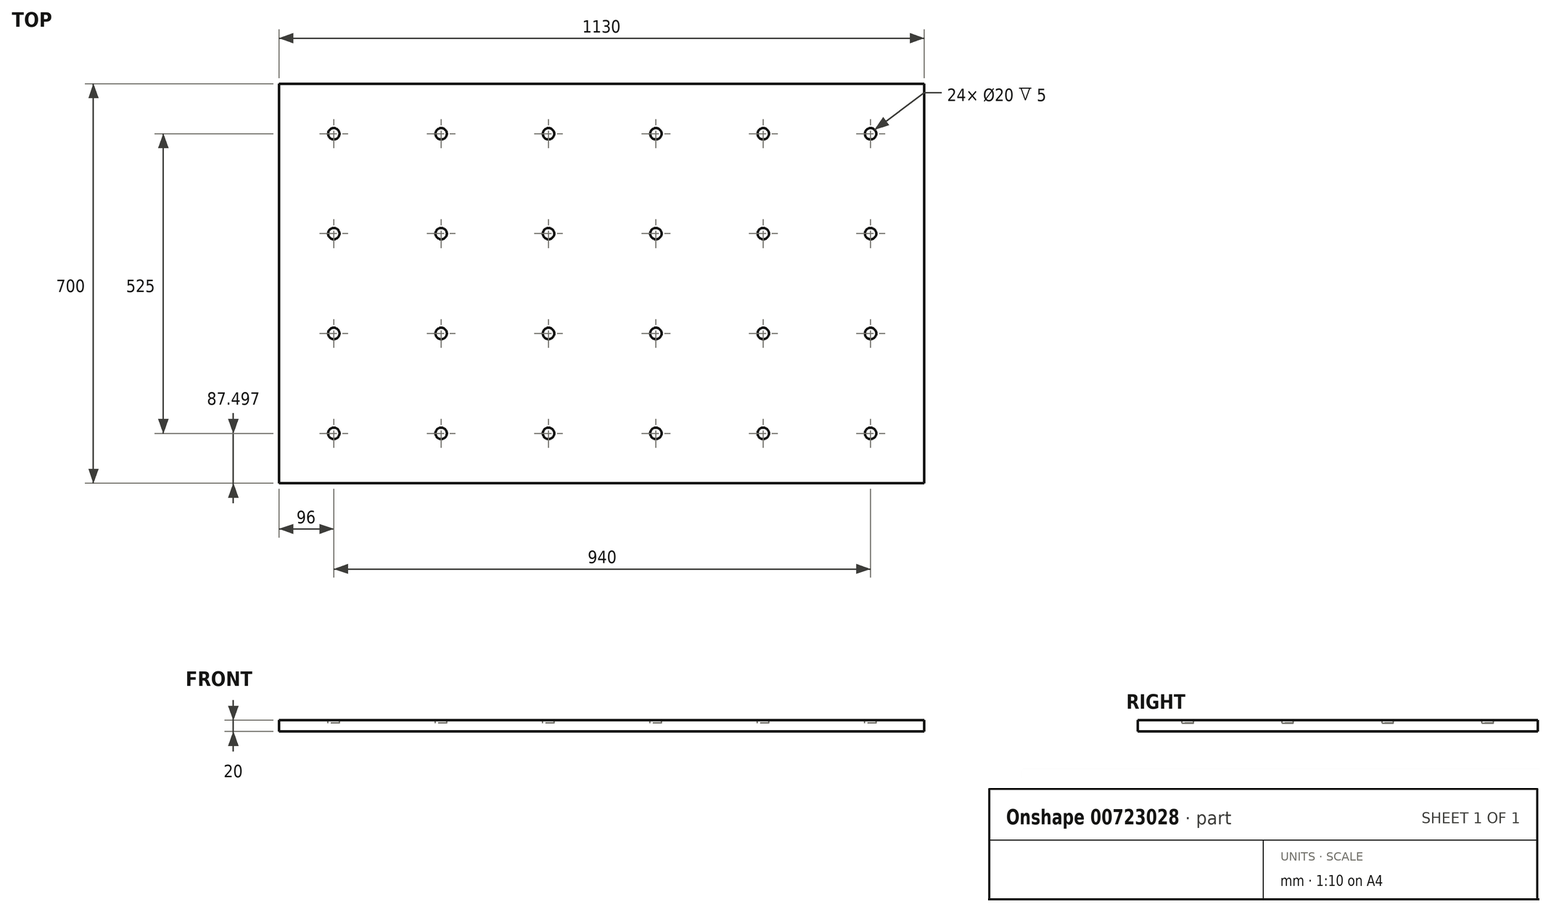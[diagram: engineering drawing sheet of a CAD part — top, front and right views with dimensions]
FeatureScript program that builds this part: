
annotation { "Feature Type Name" : "Feature", "Feature Type Description" : "" }
export const myFeature = defineFeature(function(context is Context, id is Id, definition is map)
    precondition{}
    {
        {
            var Q0;
            Q0=qCreatedBy(makeId("Top.planeOp"),FACE);
            var sketch = newSketch(context, id + "F0", { "sketchPlane" : qUnion([Q0])});
            skLineSegment(sketch, "E0.bottom", {"start": v(-556.11, 310.45) * mm, "end": v(573.89, 310.45) * mm});
            skLineSegment(sketch, "E0.top", {"start": v(-556.11, -389.55) * mm, "end": v(573.89, -389.55) * mm});
            skLineSegment(sketch, "E0.left", {"start": v(-556.11, 310.45) * mm, "end": v(-556.11, -389.55) * mm});
            skLineSegment(sketch, "E0.right", {"start": v(573.89, 310.45) * mm, "end": v(573.89, -389.55) * mm});
            skSolve(sketch);
        }
        {
            var Q0;
            Q0=makeQuery(id+"F0.imprint","IMPRINT",FACE,{"disambiguationData":[TD([[makeQuery(id+"F0.imprint","IMPRINT",EDGE,{"derivedFrom":sQuery(id+"F0.wireOp",EDGE,"E0.bottom")}),-1.0]])]});
            extrude(context, id + "F1", {"entities" : qUnion([Q0]), "depth" : 20 * mm, "offsetDistance" : 25 * mm});
        }
        {
            var Q0;
            Q0=makeQuery(id+"F1.opExtrude","CAP_FACE",FACE,{"disambiguationData":[OSD([sQuery(id+"F0.wireOp",EDGE,"E0.bottom"),sQuery(id+"F0.wireOp",EDGE,"E0.top"),sQuery(id+"F0.wireOp",EDGE,"E0.left"),sQuery(id+"F0.wireOp",EDGE,"E0.right")])],"isStart":false});
            var sketch = newSketch(context, id + "F2", { "sketchPlane" : qUnion([Q0])});
            skCircle(sketch, "E1", {"center": v(479.89, 222.95) * mm, "radius": 10 * mm});
            skCircle(sketch, "E2", {"center": v(291.89, 222.95) * mm, "radius": 10 * mm});
            skCircle(sketch, "E3", {"center": v(103.89, 222.95) * mm, "radius": 10 * mm});
            skCircle(sketch, "E4", {"center": v(-84.11, 222.95) * mm, "radius": 10 * mm});
            skCircle(sketch, "E5", {"center": v(-272.11, 222.95) * mm, "radius": 10 * mm});
            skCircle(sketch, "E6", {"center": v(-460.11, 222.95) * mm, "radius": 10 * mm});
            skCircle(sketch, "E7", {"center": v(-460.11, 47.95) * mm, "radius": 10 * mm});
            skCircle(sketch, "E8", {"center": v(-460.11, -127.05) * mm, "radius": 10 * mm});
            skCircle(sketch, "E9", {"center": v(-460.11, -302.05) * mm, "radius": 10 * mm});
            skCircle(sketch, "E10", {"center": v(-272.11, -302.05) * mm, "radius": 10 * mm});
            skCircle(sketch, "E11", {"center": v(-84.11, -302.05) * mm, "radius": 10 * mm});
            skCircle(sketch, "E12", {"center": v(103.89, -302.05) * mm, "radius": 10 * mm});
            skCircle(sketch, "E13", {"center": v(291.89, -302.05) * mm, "radius": 10 * mm});
            skCircle(sketch, "E14", {"center": v(479.89, -302.05) * mm, "radius": 10 * mm});
            skCircle(sketch, "E15", {"center": v(479.89, -127.05) * mm, "radius": 10 * mm});
            skCircle(sketch, "E16", {"center": v(479.89, 47.95) * mm, "radius": 10 * mm});
            skCircle(sketch, "E17", {"center": v(291.89, 47.95) * mm, "radius": 10 * mm});
            skCircle(sketch, "E18", {"center": v(291.89, -127.05) * mm, "radius": 10 * mm});
            skCircle(sketch, "E19", {"center": v(103.89, -127.05) * mm, "radius": 10 * mm});
            skCircle(sketch, "E20", {"center": v(-84.11, -127.05) * mm, "radius": 10 * mm});
            skCircle(sketch, "E21", {"center": v(-272.11, -127.05) * mm, "radius": 10 * mm});
            skCircle(sketch, "E22", {"center": v(-272.11, 47.95) * mm, "radius": 10 * mm});
            skCircle(sketch, "E23", {"center": v(-84.11, 47.95) * mm, "radius": 10 * mm});
            skCircle(sketch, "E24", {"center": v(103.89, 47.95) * mm, "radius": 10 * mm});
            skSolve(sketch);
        }
        {
            var Q0;
            Q0=makeQuery(id+"F2.imprint","IMPRINT",FACE,{"disambiguationData":[TD([[makeQuery(id+"F2.imprint","IMPRINT",EDGE,{"derivedFrom":sQuery(id+"F2.wireOp",EDGE,"E1")}),1.0]])]});
            var Q1;
            Q1=sQuery(id+"F2.wireOp",EDGE,"E1");
            extrude(context, id + "F3", {"entities" : qUnion([Q0]), "operationType" : NewBodyOperationType.REMOVE, "surfaceEntities" : qUnion([Q1]), "oppositeDirection" : true, "depth" : 5 * mm, "offsetDistance" : 25 * mm});
        }
        {
            var Q0;
            Q0 = qSketchRegion(id + "F2", true);
            extrude(context, id + "F4", {"entities" : qUnion([Q0]), "operationType" : NewBodyOperationType.REMOVE, "oppositeDirection" : true, "depth" : 5 * mm, "offsetDistance" : 25 * mm});
        }
    });
